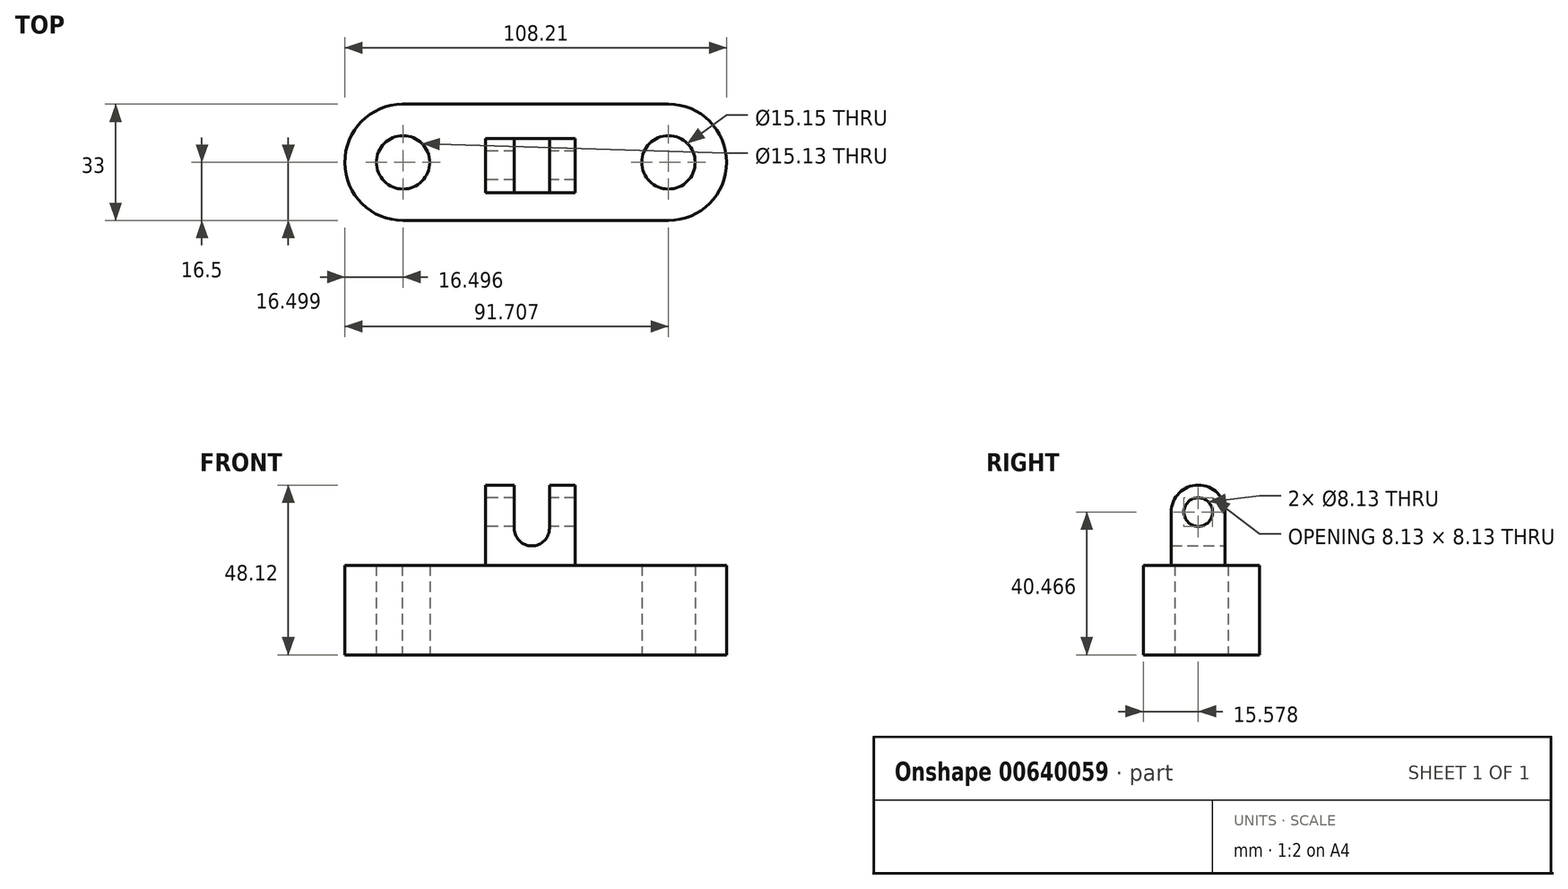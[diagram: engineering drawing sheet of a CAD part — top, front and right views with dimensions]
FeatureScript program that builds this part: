
annotation { "Feature Type Name" : "Feature", "Feature Type Description" : "" }
export const myFeature = defineFeature(function(context is Context, id is Id, definition is map)
    precondition{}
    {
        {
            var Q0;
            Q0=qCreatedBy(makeId("Top.planeOp"),FACE);
            var sketch = newSketch(context, id + "F0", { "sketchPlane" : qUnion([Q0])});
            skLineSegment(sketch, "E0", {"start": v(-29.4, 15.2) * mm, "end": v(46, 15.2) * mm});
            skLineSegment(sketch, "E1", {"start": v(46, 15.2) * mm, "end": v(46, -17.8) * mm});
            skLineSegment(sketch, "E2", {"start": v(46, -17.8) * mm, "end": v(-29.21, -17.8) * mm});
            skLineSegment(sketch, "E3", {"start": v(-29.21, -17.8) * mm, "end": v(-29.4, 15.2) * mm});
            skArc(sketch, "E4", {"start": v(-29.4, 15.2) * mm, "mid": v(-45.71, -1.39) * mm, "end": v(-29.21, -17.8) * mm});
            skArc(sketch, "E5", {"start": v(46, -17.8) * mm, "mid": v(62.5, -1.3) * mm, "end": v(46, 15.2) * mm});
            skCircle(sketch, "E6", {"center": v(-29.21, -1.29) * mm, "radius": 7.57 * mm});
            skCircle(sketch, "E7", {"center": v(46, -1.3) * mm, "radius": 7.57 * mm});
            skSolve(sketch);
        }
        {
            var Q0;
            {var subQ5=sQuery(id+"F0.wireOp",EDGE,"E0");Q0=makeQuery(id+"F0.imprint","IMPRINT",FACE,{"disambiguationData":[TD([[makeQuery(id+"F0.imprint","IMPRINT",EDGE,{"derivedFrom":subQ5}),-1.0]])]});}
            var Q1;
            {var subQ0=sQuery(id+"F0.wireOp",EDGE,"E4");Q1=makeQuery(id+"F0.imprint","IMPRINT",FACE,{"disambiguationData":[TD([[makeQuery(id+"F0.imprint","IMPRINT",EDGE,{"derivedFrom":subQ0}),1.0]])]});}
            var Q2;
            {var subQ0=sQuery(id+"F0.wireOp",EDGE,"E5");Q2=makeQuery(id+"F0.imprint","IMPRINT",FACE,{"disambiguationData":[TD([[makeQuery(id+"F0.imprint","IMPRINT",EDGE,{"derivedFrom":subQ0}),1.0]])]});}
            extrude(context, id + "F1", {"entities" : qUnion([Q0, Q1, Q2]), "depth" : 25.4 * mm, "offsetDistance" : 25.4 * mm});
        }
        {
            var Q0;
            Q0=qCreatedBy(makeId("Right.planeOp"),FACE);
            var sketch = newSketch(context, id + "F2", { "sketchPlane" : qUnion([Q0])});
            skLineSegment(sketch, "E8", {"start": v(-9.86, 25.35) * mm, "end": v(-9.86, 40.47) * mm});
            skLineSegment(sketch, "E9", {"start": v(-9.86, 40.47) * mm, "end": v(5.44, 40.47) * mm});
            skArc(sketch, "E10", {"start": v(5.44, 40.47) * mm, "mid": v(-2.21, 48.12) * mm, "end": v(-9.86, 40.47) * mm});
            skLineSegment(sketch, "E11", {"start": v(5.44, 40.47) * mm, "end": v(5.44, 25.16) * mm});
            skLineSegment(sketch, "E12", {"start": v(5.44, 25.16) * mm, "end": v(-9.86, 25.35) * mm});
            skSolve(sketch);
        }
        {
            var Q0;
            Q0=makeQuery(id+"F2.imprint","IMPRINT",FACE,{"disambiguationData":[TD([[makeQuery(id+"F2.imprint","IMPRINT",EDGE,{"derivedFrom":sQuery(id+"F2.wireOp",EDGE,"E8")}),-1.0]])]});
            var Q1;
            Q1=makeQuery(id+"F2.imprint","IMPRINT",FACE,{"disambiguationData":[TD([[makeQuery(id+"F2.imprint","IMPRINT",EDGE,{"derivedFrom":sQuery(id+"F2.wireOp",EDGE,"E9")}),1.0]])]});
            extrude(context, id + "F3", {"entities" : qUnion([Q0, Q1]), "endBound" : BoundingType.SYMMETRIC, "oppositeDirection" : true, "depth" : 25.4 * mm, "offsetDistance" : 25.4 * mm});
        }
        {
            var Q0;
            Q0=makeQuery(id+"F1.opExtrude","SWEPT_BODY",BODY,{"disambiguationData":[OSD([sQuery(id+"F0.wireOp",EDGE,"E0"),sQuery(id+"F0.wireOp",EDGE,"E2"),sQuery(id+"F0.wireOp",EDGE,"E4"),sQuery(id+"F0.wireOp",EDGE,"E5"),sQuery(id+"F0.wireOp",EDGE,"E6"),sQuery(id+"F0.wireOp",EDGE,"E7")])]});
            transform(context, id + "F4", {"entities" : qUnion([Q0]), "transformType" : TransformType.TRANSLATION_3D, "dx" : 0 * mm, "dy" : 0 * mm, "dz" : 0 * mm, "makeCopy" : false});
        }
        {
            var Q0;
            Q0=makeQuery(id+"F3.opExtrude","SWEPT_BODY",BODY,{"disambiguationData":[OSD([sQuery(id+"F2.wireOp",EDGE,"E8"),sQuery(id+"F2.wireOp",EDGE,"E10"),sQuery(id+"F2.wireOp",EDGE,"E11"),sQuery(id+"F2.wireOp",EDGE,"E12")])]});
            transform(context, id + "F5", {"entities" : qUnion([Q0]), "transformType" : TransformType.TRANSLATION_3D, "dx" : 6.86 * mm, "dy" : 0 * mm, "dz" : 0 * mm, "makeCopy" : false});
        }
        {
            var Q0;
            Q0=qCreatedBy(makeId("Front.planeOp"),FACE);
            var sketch = newSketch(context, id + "F6", { "sketchPlane" : qUnion([Q0])});
            skLineSegment(sketch, "E13", {"start": v(2.3, 51.71) * mm, "end": v(2.3, 35.86) * mm});
            skLineSegment(sketch, "E14", {"start": v(2.3, 35.86) * mm, "end": v(12.26, 35.86) * mm});
            skLineSegment(sketch, "E15", {"start": v(12.26, 35.86) * mm, "end": v(12.26, 51.71) * mm});
            skLineSegment(sketch, "E16", {"start": v(12.26, 51.71) * mm, "end": v(2.3, 51.71) * mm});
            skArc(sketch, "E17", {"start": v(2.3, 35.86) * mm, "mid": v(7.28, 30.88) * mm, "end": v(12.26, 35.86) * mm});
            skSolve(sketch);
        }
        {
            var Q0;
            Q0 = qSketchRegion(id + "F6", true);
            extrude(context, id + "F7", {"entities" : qUnion([Q0]), "operationType" : NewBodyOperationType.REMOVE, "endBound" : BoundingType.SYMMETRIC, "depth" : 25.4 * mm, "offsetDistance" : 25.4 * mm});
        }
        {
            var Q0;
            Q0=makeQuery(id+"F3.opExtrude","CAP_FACE",FACE,{"disambiguationData":[OSD([sQuery(id+"F2.wireOp",EDGE,"E8"),sQuery(id+"F2.wireOp",EDGE,"E10"),sQuery(id+"F2.wireOp",EDGE,"E11"),sQuery(id+"F2.wireOp",EDGE,"E12")])],"isStart":false});
            var sketch = newSketch(context, id + "F8", { "sketchPlane" : qUnion([Q0])});
            skCircle(sketch, "E18", {"center": v(2.21, 40.47) * mm, "radius": 4.07 * mm});
            skSolve(sketch);
        }
        {
            var Q0;
            Q0 = qSketchRegion(id + "F8", true);
            extrude(context, id + "F9", {"entities" : qUnion([Q0]), "operationType" : NewBodyOperationType.REMOVE, "oppositeDirection" : true, "depth" : 25.65 * mm, "offsetDistance" : 25.4 * mm});
        }
    });
